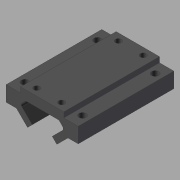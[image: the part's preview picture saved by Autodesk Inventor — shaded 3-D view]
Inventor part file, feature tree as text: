
AUTODESK INVENTOR PART (.ipt)
format: ipt  version: 2020 (Build 240168000, 168)  size: 385,536 bytes
history: native  units: in
note: dims shown in document units (in); Inventor stores cm internally (conversion verified against a paired STEP export)
features: extrude x12, sketch x11, projected_geometry x11, plane x5, mirror x3, other x2, fillet x1
ambient origin geometry x8: Origin, YZ Plane, XZ Plane, XY Plane, X Axis, Y Axis, Z Axis, Center Point
bodies: Solid3 (feature_tree)
feature tree (45):
  extrude  "Carriage Frame"  Depth=0.8661in
  fillet  "Fillet1"  Radius=0.2756in
  sketch  "Sketch7"  dims[d16=5.0in d17=0.0in]
  extrude  "Carriage Screw"  TaperAngle=0.0deg  [1 undecoded]
  other  "Ball Bearings"
  other  "Carriage Mid Plane"
  extrude  "Ball Bearing Hole"  Depth=0.125in
  mirror  "Mirror4"
  extrude  "Extrusion20"  Depth=0.378in
  extrude  "Extrusion16"  Depth=0.315in
  plane  "Work Plane6"
  extrude  "Extrusion17"  Depth=1.0in
  sketch  "Sketch21"  dims[d118=0.0in d119=0.0in d120=1.0in d121=0.0in]
  extrude  "Extrusion18"  Depth=0.06in TaperAngle=0.0deg
  extrude  "Extrusion19"  Depth=1.6in TaperAngle=0.0deg
  extrude  "Extrusion11"  Depth=0.8in TaperAngle=0.0deg
  plane  "Work Plane3"
  extrude  "Extrusion12"  Depth=1.0in TaperAngle=0.0deg
  extrude  "Extrusion13"  TaperAngle=0.0deg  [1 undecoded]
  extrude  "Extrusion14"  TaperAngle=0.0deg  [1 undecoded]
  plane  "Work Plane4"
  plane  "Work Plane5"
  mirror  "Mirror5"
  mirror  "Mirror6"
  plane  "Work Plane2"
  sketch  "Sketch12"  dims[d60=0.125in d61=0.6in]
  sketch  "Sketch1"  dims[d2=1.0in d3=1.0in d6=0.8661in d14=0.2756in]
  projected_geometry  "Projected Loop13"
  projected_geometry  "Projected Loop14"
  projected_geometry  "Projected Loop15"
  projected_geometry  "Projected Loop17"
  projected_geometry  "Projected Loop19"
  sketch  "Sketch13"  dims[d78=0.5725in d79=0.378in]
  projected_geometry  "Projected Loop20"
  sketch  "Sketch15"  dims[d80=0.0in d81=0.0in d92=0.315in]
  projected_geometry  "Projected Loop22"
  sketch  "Sketch16"  dims[d94=0.315in d106=1.0in]
  sketch  "Sketch17"  dims[d107=0.3in d110=0.06in d111=0.0in]
  projected_geometry  "Projected Loop23"
  sketch  "Sketch19"  dims[d112=0.25in d113=1.6in d114=0.0in]
  projected_geometry  "Projected Loop25"
  sketch  "Sketch20"  dims[d115=-0.6in d116=0.8in d117=0.0in]
  projected_geometry  "Projected Loop26"
  projected_geometry  "Projected Loop27"
  sketch  "Sketch23"  dims[d122=0.315in d123=0.0in d124=0.0in d127=0.0in d128=0.0in d131=1.0in d132=0.5in d133=5.0in d134=0.0in d135=0.573in d136=0.378in d137=0.0in d138=0.0in d139=0.33in d140=0.0in d141=0.315in d142=0.6569in d143=0.0in d144=1.3in d26=0.5in d27=0.0344in d28=0.5in d29=0.0344in d30=0.25in d31=0.375in d32=0.5635in d33=0.75in d34=0.8108in d35=0.0625in d36=0.75in d37=0.375in d82=0.5in d83=0.0344in]
note: 3 required parameter values undecoded (feature->parameter linkage not recoverable at this tier; creation-order binding heuristic only, values carry confidence <= 0.55)
